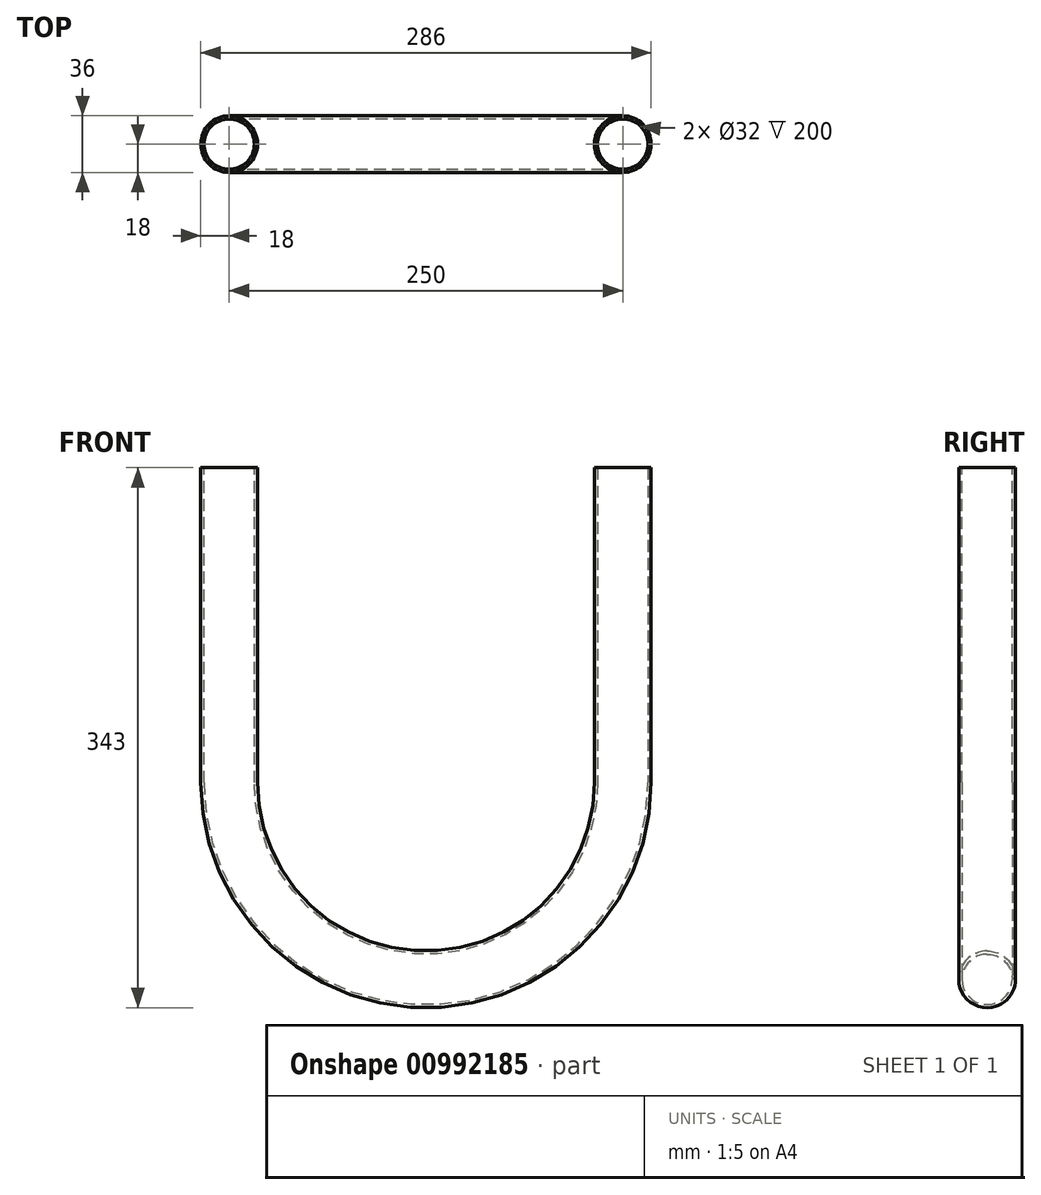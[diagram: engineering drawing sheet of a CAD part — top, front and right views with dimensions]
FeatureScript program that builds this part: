
annotation { "Feature Type Name" : "Feature", "Feature Type Description" : "" }
export const myFeature = defineFeature(function(context is Context, id is Id, definition is map)
    precondition{}
    {
        {
            var Q0;
            Q0=qCreatedBy(makeId("Front.planeOp"),FACE);
            var sketch = newSketch(context, id + "F0", { "sketchPlane" : qUnion([Q0])});
            skArc(sketch, "E0", {"start": v(-125, 0) * mm, "mid": v(0, -125) * mm, "end": v(125, 0) * mm});
            skLineSegment(sketch, "E1", {"start": v(-125, 0) * mm, "end": v(-125, 200) * mm});
            skLineSegment(sketch, "E2", {"start": v(125, 200) * mm, "end": v(125, 0) * mm});
            skSolve(sketch);
        }
        {
            var Q0;
            Q0=qCreatedBy(makeId("Top.planeOp"),FACE);
            var sketch = newSketch(context, id + "F1", { "sketchPlane" : qUnion([Q0])});
            skCircle(sketch, "E3", {"center": v(-125, 0) * mm, "radius": 18 * mm});
            skCircle(sketch, "E4", {"center": v(-125, 0) * mm, "radius": 16 * mm});
            skSolve(sketch);
        }
        {
            var Q0;
            Q0=makeQuery(id+"F1.imprint","IMPRINT",FACE,{"disambiguationData":[TD([[makeQuery(id+"F1.imprint","IMPRINT",EDGE,{"derivedFrom":sQuery(id+"F1.wireOp",EDGE,"E3")}),1.0]])]});
            var Q1;
            Q1 = qSketchRegion(id + "F0", true);
            var Q2;
            Q2=sQuery(id+"F1.wireOp",EDGE,"E3");
            var Q3;
            Q3=sQuery(id+"F1.wireOp",EDGE,"msPuSbXG-Bu3d-Jlch-ZL5n-ad25TIJzcVim");
            var Q4;
            Q4=sQuery(id+"F0.wireOp",EDGE,"E1");
            var Q5;
            Q5=sQuery(id+"F0.wireOp",EDGE,"E0");
            var Q6;
            Q6=sQuery(id+"F0.wireOp",EDGE,"E2");
            sweep(context, id + "F2", {"profiles" : qUnion([Q0, Q1]), "surfaceProfiles" : qUnion([Q2, Q3]), "path" : qUnion([Q4, Q5, Q6])});
        }
    });
